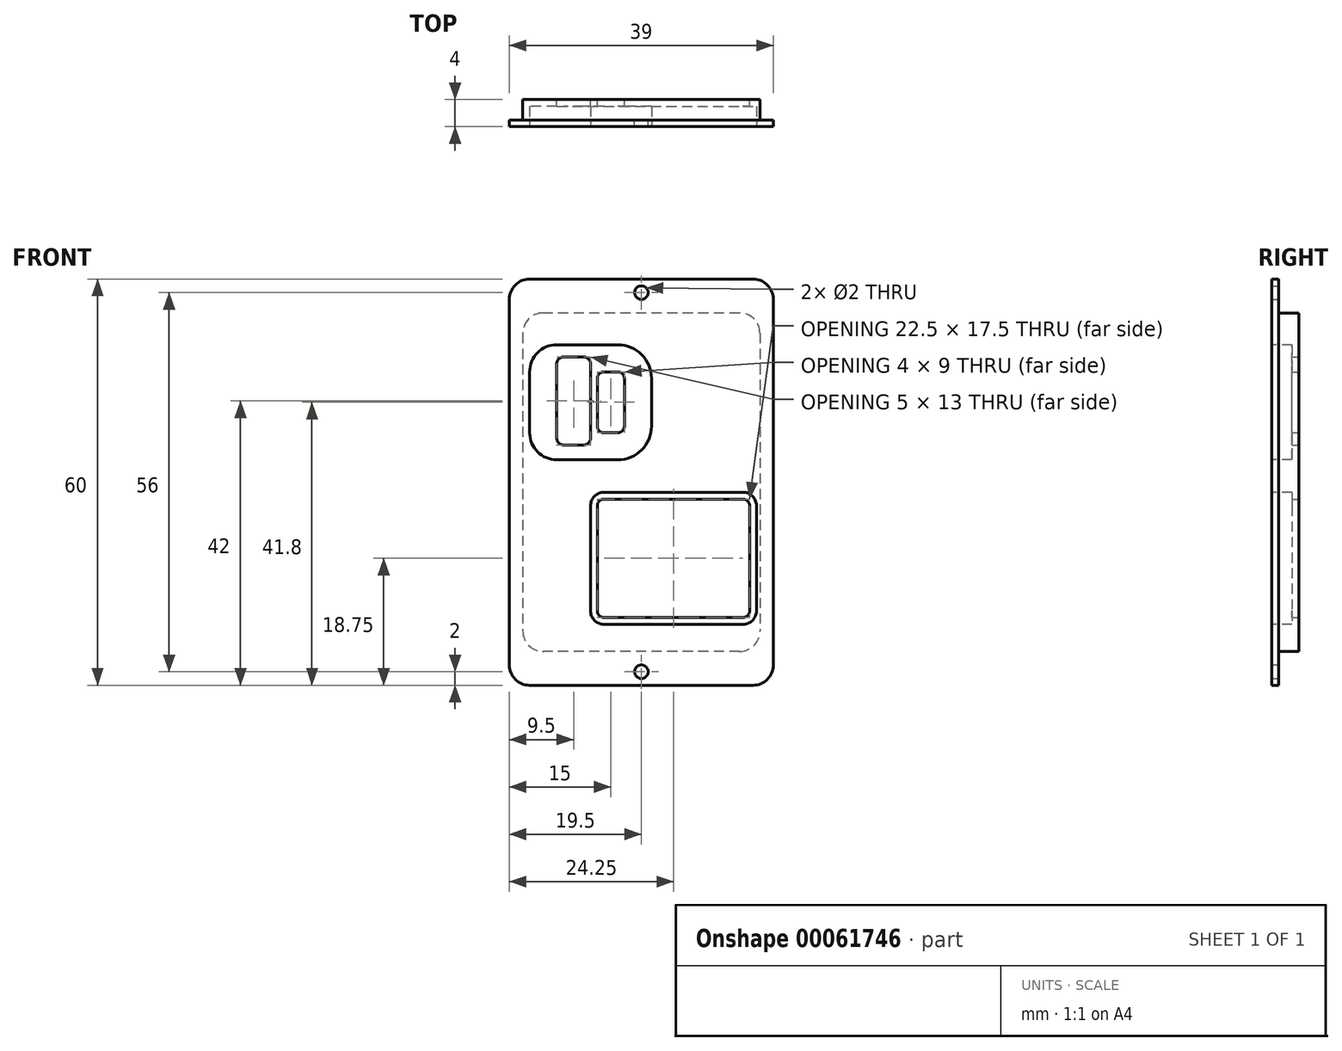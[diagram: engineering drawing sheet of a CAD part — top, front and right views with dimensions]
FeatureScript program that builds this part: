
annotation { "Feature Type Name" : "Feature", "Feature Type Description" : "" }
export const myFeature = defineFeature(function(context is Context, id is Id, definition is map)
    precondition{}
    {
        {
            var Q0;
            Q0=qCreatedBy(makeId("Front.planeOp"),FACE);
            var sketch = newSketch(context, id + "F0", { "sketchPlane" : qUnion([Q0])});
            skLineSegment(sketch, "E0.bottom", {"start": v(-16.5, 30) * mm, "end": v(16.5, 30) * mm});
            skLineSegment(sketch, "E0.top", {"start": v(-16.5, -30) * mm, "end": v(16.5, -30) * mm});
            skLineSegment(sketch, "E0.left", {"start": v(-19.5, 27) * mm, "end": v(-19.5, -27) * mm});
            skLineSegment(sketch, "E0.right", {"start": v(19.5, 27) * mm, "end": v(19.5, -27) * mm});
            skLineSegment(sketch, "E1", {"start": v(-19.5, 0) * mm, "end": v(19.5, 0) * mm, "construction": true});
            skLineSegment(sketch, "E2", {"start": v(0, 30) * mm, "end": v(0, -30) * mm, "construction": true});
            skPoint(sketch, "E3.visualSharp", {"position": v(-19.5, 30) * mm});
            skArc(sketch, "E3.filletArc", {"start": v(-16.5, 30) * mm, "mid": v(-18.62, 29.12) * mm, "end": v(-19.5, 27) * mm});
            skPoint(sketch, "E4.visualSharp", {"position": v(19.5, 30) * mm});
            skArc(sketch, "E4.filletArc", {"start": v(19.5, 27) * mm, "mid": v(18.62, 29.12) * mm, "end": v(16.5, 30) * mm});
            skPoint(sketch, "E5.visualSharp", {"position": v(19.5, -30) * mm});
            skArc(sketch, "E5.filletArc", {"start": v(16.5, -30) * mm, "mid": v(18.62, -29.12) * mm, "end": v(19.5, -27) * mm});
            skPoint(sketch, "E6.visualSharp", {"position": v(-19.5, -30) * mm});
            skArc(sketch, "E6.filletArc", {"start": v(-19.5, -27) * mm, "mid": v(-18.62, -29.12) * mm, "end": v(-16.5, -30) * mm});
            skCircle(sketch, "E7", {"center": v(0, 28) * mm, "radius": 1 * mm});
            skCircle(sketch, "E8.MirrorC", {"center": v(0, -28) * mm, "radius": 1 * mm});
            skLineSegment(sketch, "E9.bottom", {"start": v(-5.5, -2.5) * mm, "end": v(15, -2.5) * mm});
            skLineSegment(sketch, "E9.top", {"start": v(-5.5, -20) * mm, "end": v(15, -20) * mm});
            skLineSegment(sketch, "E9.right", {"start": v(16, -3.5) * mm, "end": v(16, -19) * mm});
            skLineSegment(sketch, "E10", {"start": v(-6.5, -3.5) * mm, "end": v(-6.5, -19) * mm});
            skPoint(sketch, "E11.visualSharp", {"position": v(-6.5, -20) * mm});
            skArc(sketch, "E11.filletArc", {"start": v(-6.5, -19) * mm, "mid": v(-6.2, -19.7) * mm, "end": v(-5.5, -20) * mm});
            skPoint(sketch, "E12.visualSharp", {"position": v(-6.5, -2.5) * mm});
            skArc(sketch, "E12.filletArc", {"start": v(-5.5, -2.5) * mm, "mid": v(-6.2, -2.8) * mm, "end": v(-6.5, -3.5) * mm});
            skPoint(sketch, "E13.visualSharp", {"position": v(16, -2.5) * mm});
            skArc(sketch, "E13.filletArc", {"start": v(16, -3.5) * mm, "mid": v(15.7, -2.8) * mm, "end": v(15, -2.5) * mm});
            skPoint(sketch, "E14.visualSharp", {"position": v(16, -20) * mm});
            skArc(sketch, "E14.filletArc", {"start": v(15, -20) * mm, "mid": v(15.7, -19.7) * mm, "end": v(16, -19) * mm});
            skLineSegment(sketch, "E15.bottom", {"start": v(-5.5, 7.3) * mm, "end": v(-3.5, 7.3) * mm});
            skLineSegment(sketch, "E15.top", {"start": v(-5.5, 16.3) * mm, "end": v(-3.5, 16.3) * mm});
            skLineSegment(sketch, "E15.left", {"start": v(-6.5, 8.3) * mm, "end": v(-6.5, 15.3) * mm});
            skLineSegment(sketch, "E15.right", {"start": v(-2.5, 8.3) * mm, "end": v(-2.5, 15.3) * mm});
            skPoint(sketch, "E16.visualSharp", {"position": v(-2.5, 7.3) * mm});
            skArc(sketch, "E16.filletArc", {"start": v(-3.5, 7.3) * mm, "mid": v(-2.8, 7.6) * mm, "end": v(-2.5, 8.3) * mm});
            skPoint(sketch, "E17.visualSharp", {"position": v(-6.5, 16.3) * mm});
            skArc(sketch, "E17.filletArc", {"start": v(-5.5, 16.3) * mm, "mid": v(-6.2, 16) * mm, "end": v(-6.5, 15.3) * mm});
            skPoint(sketch, "E18.visualSharp", {"position": v(-2.5, 16.3) * mm});
            skArc(sketch, "E18.filletArc", {"start": v(-2.5, 15.3) * mm, "mid": v(-2.8, 16) * mm, "end": v(-3.5, 16.3) * mm});
            skPoint(sketch, "E19.visualSharp", {"position": v(-6.5, 7.3) * mm});
            skArc(sketch, "E19.filletArc", {"start": v(-6.5, 8.3) * mm, "mid": v(-6.2, 7.6) * mm, "end": v(-5.5, 7.3) * mm});
            skLineSegment(sketch, "E20.bottom", {"start": v(-8.5, 5.5) * mm, "end": v(-11.5, 5.5) * mm});
            skLineSegment(sketch, "E20.top", {"start": v(-8.5, 18.5) * mm, "end": v(-11.5, 18.5) * mm});
            skLineSegment(sketch, "E20.left", {"start": v(-7.5, 6.5) * mm, "end": v(-7.5, 17.5) * mm});
            skLineSegment(sketch, "E20.right", {"start": v(-12.5, 6.5) * mm, "end": v(-12.5, 17.5) * mm});
            skPoint(sketch, "E21.visualSharp", {"position": v(-7.5, 5.5) * mm});
            skArc(sketch, "E21.filletArc", {"start": v(-8.5, 5.5) * mm, "mid": v(-7.8, 5.8) * mm, "end": v(-7.5, 6.5) * mm});
            skPoint(sketch, "E22.visualSharp", {"position": v(-12.5, 18.5) * mm});
            skArc(sketch, "E22.filletArc", {"start": v(-11.5, 18.5) * mm, "mid": v(-12.2, 18.2) * mm, "end": v(-12.5, 17.5) * mm});
            skPoint(sketch, "E23.visualSharp", {"position": v(-7.5, 18.5) * mm});
            skArc(sketch, "E23.filletArc", {"start": v(-7.5, 17.5) * mm, "mid": v(-7.8, 18.2) * mm, "end": v(-8.5, 18.5) * mm});
            skPoint(sketch, "E24.visualSharp", {"position": v(-12.5, 5.5) * mm});
            skArc(sketch, "E24.filletArc", {"start": v(-12.5, 6.5) * mm, "mid": v(-12.2, 5.8) * mm, "end": v(-11.5, 5.5) * mm});
            skSolve(sketch);
        }
        {
            var Q0;
            Q0=makeQuery(id+"F0.imprint","IMPRINT",FACE,{"disambiguationData":[TD([[makeQuery(id+"F0.imprint","IMPRINT",EDGE,{"derivedFrom":sQuery(id+"F0.wireOp",EDGE,"E0.bottom")}),-1.0]])]});
            extrude(context, id + "F1", {"entities" : qUnion([Q0]), "depth" : 1 * mm});
        }
        {
            var Q0;
            Q0=makeQuery(id+"F1.opExtrude","CAP_FACE",FACE,{"disambiguationData":[OSD([sQuery(id+"F0.wireOp",EDGE,"E0.bottom"),sQuery(id+"F0.wireOp",EDGE,"E0.top"),sQuery(id+"F0.wireOp",EDGE,"E0.left"),sQuery(id+"F0.wireOp",EDGE,"E0.right"),sQuery(id+"F0.wireOp",EDGE,"E3.filletArc"),sQuery(id+"F0.wireOp",EDGE,"E4.filletArc"),sQuery(id+"F0.wireOp",EDGE,"E5.filletArc"),sQuery(id+"F0.wireOp",EDGE,"E6.filletArc"),sQuery(id+"F0.wireOp",EDGE,"E7"),sQuery(id+"F0.wireOp",EDGE,"E8.MirrorC"),sQuery(id+"F0.wireOp",EDGE,"E9.bottom"),sQuery(id+"F0.wireOp",EDGE,"E9.top"),sQuery(id+"F0.wireOp",EDGE,"E9.left"),sQuery(id+"F0.wireOp",EDGE,"E9.right")])],"isStart":true});
            var sketch = newSketch(context, id + "F2", { "sketchPlane" : qUnion([Q0])});
            skLineSegment(sketch, "E25.bottom", {"start": v(-14.5, 25) * mm, "end": v(14.5, 25) * mm});
            skLineSegment(sketch, "E25.top", {"start": v(-14.5, -25) * mm, "end": v(14.5, -25) * mm});
            skLineSegment(sketch, "E25.left", {"start": v(-17.5, 22) * mm, "end": v(-17.5, -22) * mm});
            skLineSegment(sketch, "E25.right", {"start": v(17.5, 22) * mm, "end": v(17.5, -22) * mm});
            skPoint(sketch, "E26.visualSharp", {"position": v(17.5, 25) * mm});
            skArc(sketch, "E26.filletArc", {"start": v(17.5, 22) * mm, "mid": v(16.62, 24.12) * mm, "end": v(14.5, 25) * mm});
            skPoint(sketch, "E27.visualSharp", {"position": v(-17.5, 25) * mm});
            skArc(sketch, "E27.filletArc", {"start": v(-14.5, 25) * mm, "mid": v(-16.62, 24.12) * mm, "end": v(-17.5, 22) * mm});
            skPoint(sketch, "E28.visualSharp", {"position": v(-17.5, -25) * mm});
            skArc(sketch, "E28.filletArc", {"start": v(-17.5, -22) * mm, "mid": v(-16.62, -24.12) * mm, "end": v(-14.5, -25) * mm});
            skPoint(sketch, "E29.visualSharp", {"position": v(17.5, -25) * mm});
            skArc(sketch, "E29.filletArc", {"start": v(14.5, -25) * mm, "mid": v(16.62, -24.12) * mm, "end": v(17.5, -22) * mm});
            skSolve(sketch);
        }
        {
            var Q0;
            Q0=makeQuery(id+"F2.imprint","IMPRINT",FACE,{"disambiguationData":[TD([[makeQuery(id+"F2.imprint","IMPRINT",EDGE,{"derivedFrom":sQuery(id+"F2.wireOp",EDGE,"E25.bottom")}),-1.0]])]});
            extrude(context, id + "F3", {"entities" : qUnion([Q0]), "operationType" : NewBodyOperationType.ADD, "depth" : 3 * mm});
        }
        {
            var Q0;
            Q0=makeQuery(id+"F1.opExtrude","CAP_FACE",FACE,{"disambiguationData":[OSD([sQuery(id+"F0.wireOp",EDGE,"E0.bottom"),sQuery(id+"F0.wireOp",EDGE,"E0.top"),sQuery(id+"F0.wireOp",EDGE,"E0.left"),sQuery(id+"F0.wireOp",EDGE,"E0.right"),sQuery(id+"F0.wireOp",EDGE,"E3.filletArc"),sQuery(id+"F0.wireOp",EDGE,"E4.filletArc"),sQuery(id+"F0.wireOp",EDGE,"E5.filletArc"),sQuery(id+"F0.wireOp",EDGE,"E6.filletArc"),sQuery(id+"F0.wireOp",EDGE,"E7"),sQuery(id+"F0.wireOp",EDGE,"E8.MirrorC"),sQuery(id+"F0.wireOp",EDGE,"E9.bottom"),sQuery(id+"F0.wireOp",EDGE,"E9.top"),sQuery(id+"F0.wireOp",EDGE,"E9.right"),sQuery(id+"F0.wireOp",EDGE,"E10"),sQuery(id+"F0.wireOp",EDGE,"E11.filletArc"),sQuery(id+"F0.wireOp",EDGE,"E12.filletArc"),sQuery(id+"F0.wireOp",EDGE,"E13.filletArc"),sQuery(id+"F0.wireOp",EDGE,"E14.filletArc")])],"isStart":false});
            var sketch = newSketch(context, id + "F4", { "sketchPlane" : qUnion([Q0])});
            skLineSegment(sketch, "E30.0", {"start": v(-7.5, -3.5) * mm, "end": v(-7.5, -19) * mm});
            skArc(sketch, "E30.1", {"start": v(-5.5, -1.5) * mm, "mid": v(-6.91, -2.09) * mm, "end": v(-7.5, -3.5) * mm});
            skArc(sketch, "E30.2", {"start": v(-7.5, -19) * mm, "mid": v(-6.91, -20.41) * mm, "end": v(-5.5, -21) * mm});
            skLineSegment(sketch, "E30.3", {"start": v(-5.5, -1.5) * mm, "end": v(15, -1.5) * mm});
            skLineSegment(sketch, "E30.4", {"start": v(-5.5, -21) * mm, "end": v(15, -21) * mm});
            skArc(sketch, "E30.5", {"start": v(15, -21) * mm, "mid": v(16.41, -20.41) * mm, "end": v(17, -19) * mm});
            skLineSegment(sketch, "E30.6", {"start": v(17, -3.5) * mm, "end": v(17, -19) * mm});
            skArc(sketch, "E30.7", {"start": v(17, -3.5) * mm, "mid": v(16.41, -2.09) * mm, "end": v(15, -1.5) * mm});
            skLineSegment(sketch, "E31.0", {"start": v(-10.5, 8.3) * mm, "end": v(-10.5, 15.3) * mm});
            skArc(sketch, "E31.1", {"start": v(-5.5, 20.3) * mm, "mid": v(-9.04, 18.84) * mm, "end": v(-10.5, 15.3) * mm});
            skArc(sketch, "E31.2", {"start": v(-10.5, 8.3) * mm, "mid": v(-9.04, 4.76) * mm, "end": v(-5.5, 3.3) * mm});
            skLineSegment(sketch, "E31.3", {"start": v(-5.5, 20.3) * mm, "end": v(-3.5, 20.3) * mm});
            skLineSegment(sketch, "E31.4", {"start": v(-5.5, 3.3) * mm, "end": v(-3.5, 3.3) * mm});
            skArc(sketch, "E31.5", {"start": v(-3.5, 3.3) * mm, "mid": v(0.04, 4.76) * mm, "end": v(1.5, 8.3) * mm});
            skLineSegment(sketch, "E31.6", {"start": v(1.5, 8.3) * mm, "end": v(1.5, 15.3) * mm});
            skArc(sketch, "E31.7", {"start": v(1.5, 15.3) * mm, "mid": v(0.04, 18.84) * mm, "end": v(-3.5, 20.3) * mm});
            skLineSegment(sketch, "E32", {"start": v(-5.5, 3.3) * mm, "end": v(-12.5, 3.3) * mm});
            skLineSegment(sketch, "E33", {"start": v(-16.5, 7.3) * mm, "end": v(-16.5, 16.3) * mm});
            skLineSegment(sketch, "E34", {"start": v(-12.5, 20.3) * mm, "end": v(-5.5, 20.3) * mm});
            skPoint(sketch, "E35.visualSharp", {"position": v(-16.5, 3.3) * mm});
            skArc(sketch, "E35.filletArc", {"start": v(-16.5, 7.3) * mm, "mid": v(-15.33, 4.47) * mm, "end": v(-12.5, 3.3) * mm});
            skPoint(sketch, "E36.visualSharp", {"position": v(-16.5, 20.3) * mm});
            skArc(sketch, "E36.filletArc", {"start": v(-12.5, 20.3) * mm, "mid": v(-15.33, 19.13) * mm, "end": v(-16.5, 16.3) * mm});
            skSolve(sketch);
        }
        {
            var Q0;
            Q0=makeQuery(id+"F4.imprint","IMPRINT",FACE,{"disambiguationData":[TD([[makeQuery(id+"F4.imprint","IMPRINT",EDGE,{"derivedFrom":sQuery(id+"F4.wireOp",EDGE,"E30.0")}),1.0]])]});
            var Q1;
            Q1=makeQuery(id+"F4.imprint","IMPRINT",FACE,{"disambiguationData":[TD([[makeQuery(id+"F4.imprint","IMPRINT",EDGE,{"derivedFrom":sQuery(id+"F4.wireOp",EDGE,"b70a0878-04f3-466d-972c-2b75f5636668.0")}),1.0]])]});
            var Q2;
            Q2=makeQuery(id+"F4.imprint","IMPRINT",FACE,{"disambiguationData":[TD([[makeQuery(id+"F4.imprint","IMPRINT",EDGE,{"derivedFrom":sQuery(id+"F4.wireOp",EDGE,"E31.0")}),-1.0]])]});
            var Q3;
            {var subQ1=sQuery(id+"F4.wireOp",EDGE,"E32");Q3=makeQuery(id+"F4.imprint","IMPRINT",FACE,{"disambiguationData":[TD([[makeQuery(id+"F4.imprint","IMPRINT",EDGE,{"derivedFrom":subQ1}),-1.0]])]});}
            var Q4;
            {var subQ1=sQuery(id+"F4.wireOp",EDGE,"E31.3");Q4=makeQuery(id+"F4.imprint","IMPRINT",FACE,{"disambiguationData":[TD([[makeQuery(id+"F4.imprint","IMPRINT",EDGE,{"derivedFrom":subQ1}),-1.0]])]});}
            extrude(context, id + "F5", {"entities" : qUnion([Q0, Q1, Q2, Q3, Q4]), "operationType" : NewBodyOperationType.REMOVE, "oppositeDirection" : true, "depth" : 3 * mm});
        }
    });
